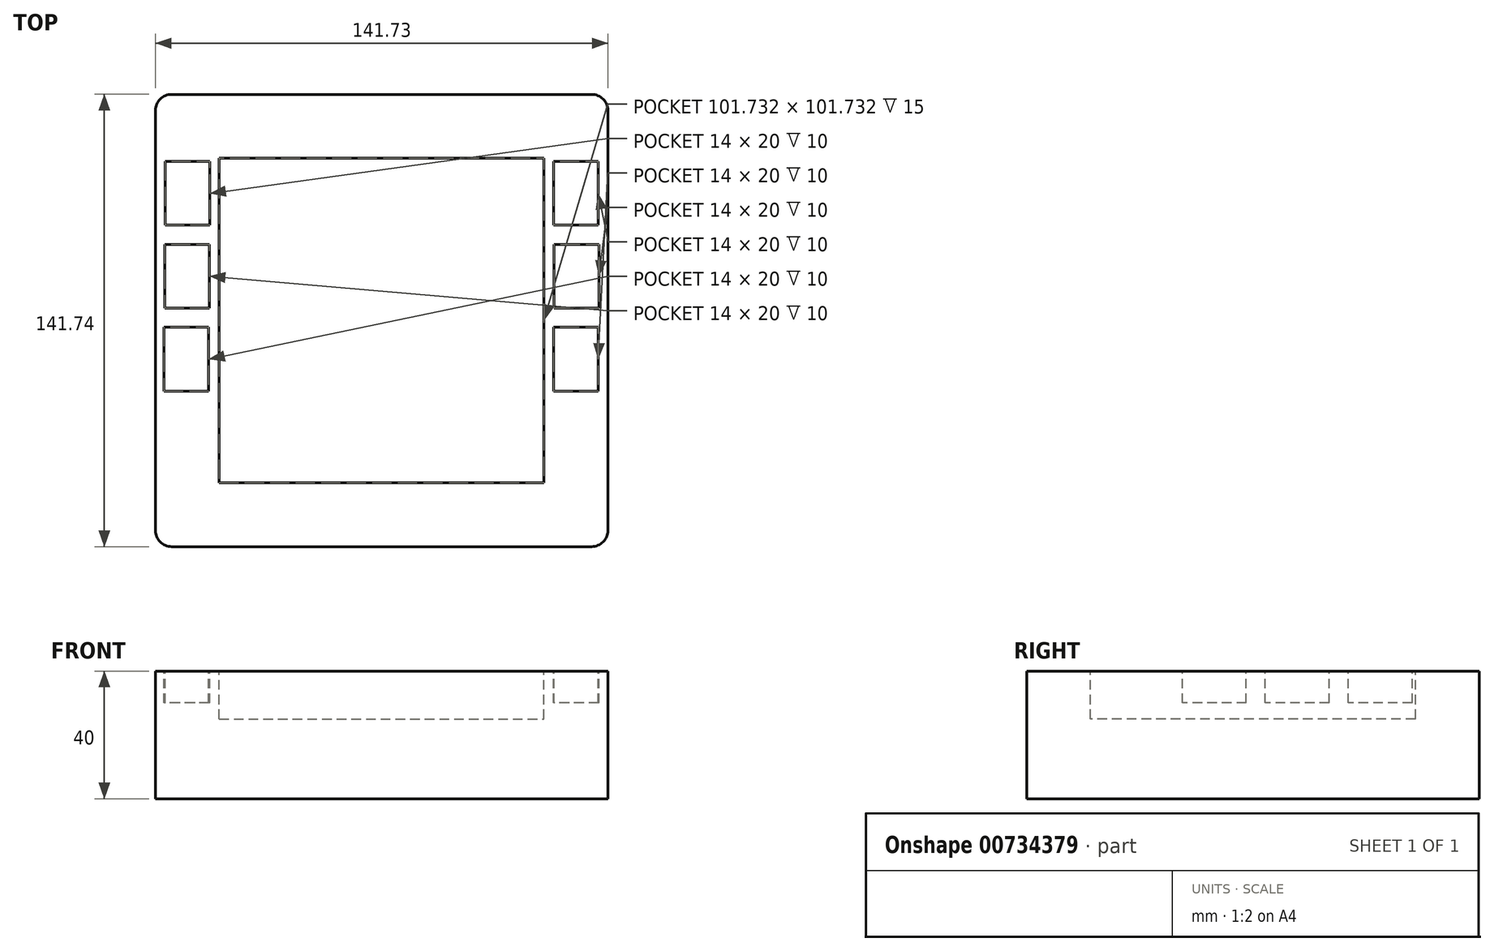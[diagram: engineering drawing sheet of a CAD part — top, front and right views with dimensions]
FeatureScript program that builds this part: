
annotation { "Feature Type Name" : "Feature", "Feature Type Description" : "" }
export const myFeature = defineFeature(function(context is Context, id is Id, definition is map)
    precondition{}
    {
        {
            var Q0;
            Q0=qCreatedBy(makeId("Top.planeOp"),FACE);
            var sketch = newSketch(context, id + "F0", { "sketchPlane" : qUnion([Q0])});
            skLineSegment(sketch, "E0.bottom", {"start": v(-71.65, 70.87) * mm, "end": v(59.92, 70.87) * mm});
            skLineSegment(sketch, "E0.top", {"start": v(-71.65, -70.87) * mm, "end": v(59.92, -70.87) * mm});
            skLineSegment(sketch, "E0.left", {"start": v(-76.73, 65.79) * mm, "end": v(-76.73, -65.79) * mm});
            skLineSegment(sketch, "E0.right", {"start": v(65, 65.79) * mm, "end": v(65, -65.79) * mm});
            skArc(sketch, "E1", {"start": v(-71.65, 70.87) * mm, "mid": v(-75.24, 69.38) * mm, "end": v(-76.73, 65.79) * mm});
            skArc(sketch, "E2", {"start": v(59.92, -70.87) * mm, "mid": v(63.51, -69.38) * mm, "end": v(65, -65.79) * mm});
            skArc(sketch, "E3", {"start": v(-76.73, -65.79) * mm, "mid": v(-75.24, -69.38) * mm, "end": v(-71.65, -70.87) * mm});
            skArc(sketch, "E4", {"start": v(65, 65.79) * mm, "mid": v(63.51, 69.38) * mm, "end": v(59.92, 70.87) * mm});
            skSolve(sketch);
        }
        {
            var Q0;
            Q0 = qSketchRegion(id + "F0", true);
            extrude(context, id + "F1", {"entities" : qUnion([Q0]), "depth" : 40 * mm, "offsetDistance" : 25.4 * mm});
        }
        {
            var Q0;
            Q0=makeQuery(id+"F1.opExtrude","CAP_FACE",FACE,{"disambiguationData":[OSD([sQuery(id+"F0.wireOp",EDGE,"E0.bottom"),sQuery(id+"F0.wireOp",EDGE,"E0.top"),sQuery(id+"F0.wireOp",EDGE,"E0.left"),sQuery(id+"F0.wireOp",EDGE,"E0.right"),sQuery(id+"F0.wireOp",EDGE,"E1"),sQuery(id+"F0.wireOp",EDGE,"E2"),sQuery(id+"F0.wireOp",EDGE,"E3"),sQuery(id+"F0.wireOp",EDGE,"E4")])],"isStart":false});
            var sketch = newSketch(context, id + "F2", { "sketchPlane" : qUnion([Q0])});
            skLineSegment(sketch, "E5.bottom", {"start": v(-56.73, 50.87) * mm, "end": v(45, 50.87) * mm});
            skLineSegment(sketch, "E5.top", {"start": v(-56.73, -50.87) * mm, "end": v(45, -50.87) * mm});
            skLineSegment(sketch, "E5.left", {"start": v(-56.73, 50.87) * mm, "end": v(-56.73, -50.87) * mm});
            skLineSegment(sketch, "E5.right", {"start": v(45, 50.87) * mm, "end": v(45, -50.87) * mm});
            skSolve(sketch);
        }
        {
            var Q0;
            Q0 = qSketchRegion(id + "F2", true);
            extrude(context, id + "F3", {"entities" : qUnion([Q0]), "operationType" : NewBodyOperationType.REMOVE, "oppositeDirection" : true, "depth" : 15 * mm, "offsetDistance" : 25.4 * mm});
        }
        {
            var Q0;
            Q0=makeQuery(id+"F1.opExtrude","CAP_FACE",FACE,{"disambiguationData":[OSD([sQuery(id+"F0.wireOp",EDGE,"E0.bottom"),sQuery(id+"F0.wireOp",EDGE,"E0.top"),sQuery(id+"F0.wireOp",EDGE,"E0.left"),sQuery(id+"F0.wireOp",EDGE,"E0.right"),sQuery(id+"F0.wireOp",EDGE,"E1"),sQuery(id+"F0.wireOp",EDGE,"E2"),sQuery(id+"F0.wireOp",EDGE,"E3"),sQuery(id+"F0.wireOp",EDGE,"E4")])],"isStart":false});
            var sketch = newSketch(context, id + "F4", { "sketchPlane" : qUnion([Q0])});
            skLineSegment(sketch, "E6.bottom", {"start": v(-59.73, 49.86) * mm, "end": v(-73.73, 49.86) * mm});
            skLineSegment(sketch, "E6.top", {"start": v(-59.73, 29.86) * mm, "end": v(-73.73, 29.86) * mm});
            skLineSegment(sketch, "E6.left", {"start": v(-59.73, 49.86) * mm, "end": v(-59.73, 29.86) * mm});
            skLineSegment(sketch, "E6.right", {"start": v(-73.73, 49.86) * mm, "end": v(-73.73, 29.86) * mm});
            skLineSegment(sketch, "E7.bottom", {"start": v(-59.86, 23.86) * mm, "end": v(-73.86, 23.86) * mm});
            skLineSegment(sketch, "E7.top", {"start": v(-59.86, 3.86) * mm, "end": v(-73.86, 3.86) * mm});
            skLineSegment(sketch, "E7.left", {"start": v(-59.86, 23.86) * mm, "end": v(-59.86, 3.86) * mm});
            skLineSegment(sketch, "E7.right", {"start": v(-73.86, 23.86) * mm, "end": v(-73.86, 3.86) * mm});
            skLineSegment(sketch, "E8.bottom", {"start": v(-60.03, -2.14) * mm, "end": v(-74.03, -2.14) * mm});
            skLineSegment(sketch, "E8.top", {"start": v(-60.03, -22.14) * mm, "end": v(-74.03, -22.14) * mm});
            skLineSegment(sketch, "E8.left", {"start": v(-60.03, -2.14) * mm, "end": v(-60.03, -22.14) * mm});
            skLineSegment(sketch, "E8.right", {"start": v(-74.03, -2.14) * mm, "end": v(-74.03, -22.14) * mm});
            skLineSegment(sketch, "E9.bottom", {"start": v(62, 49.86) * mm, "end": v(48, 49.86) * mm});
            skLineSegment(sketch, "E9.top", {"start": v(62, 29.86) * mm, "end": v(48, 29.86) * mm});
            skLineSegment(sketch, "E9.left", {"start": v(62, 49.86) * mm, "end": v(62, 29.86) * mm});
            skLineSegment(sketch, "E9.right", {"start": v(48, 49.86) * mm, "end": v(48, 29.86) * mm});
            skLineSegment(sketch, "E10.bottom", {"start": v(62.17, 23.86) * mm, "end": v(48.17, 23.86) * mm});
            skLineSegment(sketch, "E10.top", {"start": v(62.17, 3.86) * mm, "end": v(48.17, 3.86) * mm});
            skLineSegment(sketch, "E10.left", {"start": v(62.17, 23.86) * mm, "end": v(62.17, 3.86) * mm});
            skLineSegment(sketch, "E10.right", {"start": v(48.17, 23.86) * mm, "end": v(48.17, 3.86) * mm});
            skLineSegment(sketch, "E11.bottom", {"start": v(62, -2.14) * mm, "end": v(48, -2.14) * mm});
            skLineSegment(sketch, "E11.top", {"start": v(62, -22.14) * mm, "end": v(48, -22.14) * mm});
            skLineSegment(sketch, "E11.left", {"start": v(62, -2.14) * mm, "end": v(62, -22.14) * mm});
            skLineSegment(sketch, "E11.right", {"start": v(48, -2.14) * mm, "end": v(48, -22.14) * mm});
            skSolve(sketch);
        }
        {
            var Q0;
            Q0 = qSketchRegion(id + "F4", true);
            extrude(context, id + "F5", {"entities" : qUnion([Q0]), "operationType" : NewBodyOperationType.REMOVE, "oppositeDirection" : true, "depth" : 10 * mm, "offsetDistance" : 25 * mm});
        }
    });
